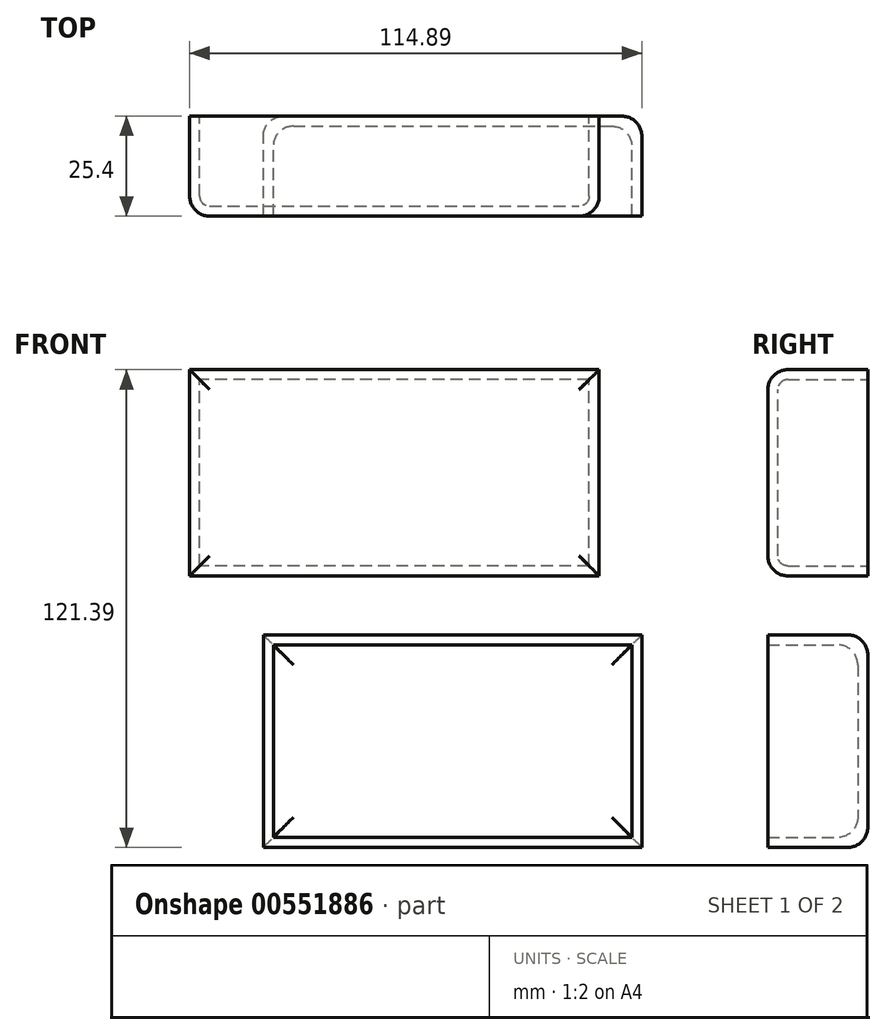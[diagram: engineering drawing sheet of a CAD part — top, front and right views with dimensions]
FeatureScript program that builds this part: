
annotation { "Feature Type Name" : "Feature", "Feature Type Description" : "" }
export const myFeature = defineFeature(function(context is Context, id is Id, definition is map)
    precondition{}
    {
        {
            var Q0;
            Q0=qCreatedBy(makeId("Front.planeOp"),FACE);
            var sketch = newSketch(context, id + "F0", { "sketchPlane" : qUnion([Q0])});
            skLineSegment(sketch, "E0.bottom", {"start": v(29.76, 10.05) * mm, "end": v(-74.3, 10.05) * mm});
            skLineSegment(sketch, "E0.top", {"start": v(29.76, 62.47) * mm, "end": v(-74.3, 62.47) * mm});
            skLineSegment(sketch, "E0.left", {"start": v(29.76, 10.05) * mm, "end": v(29.76, 62.47) * mm});
            skLineSegment(sketch, "E0.right", {"start": v(-74.3, 10.05) * mm, "end": v(-74.3, 62.47) * mm});
            skPoint(sketch, "E0.middle", {"position": v(-22.27, 36.26) * mm});
            skSolve(sketch);
        }
        {
            var Q0;
            Q0 = qSketchRegion(id + "F0", true);
            extrude(context, id + "F1", {"entities" : qUnion([Q0]), "depth" : 25.4 * mm, "offsetDistance" : 25.4 * mm});
        }
        {
            var Q0;
            Q0=makeQuery(id+"F1.opExtrude","CAP_FACE",FACE,{"disambiguationData":[OSD([sQuery(id+"F0.wireOp",EDGE,"E0.bottom"),sQuery(id+"F0.wireOp",EDGE,"E0.top"),sQuery(id+"F0.wireOp",EDGE,"E0.left"),sQuery(id+"F0.wireOp",EDGE,"E0.right")])],"isStart":false});
            fillet(context, id + "F2", {"entities" : qUnion([Q0]), "radius" : 5.08 * mm, "tangentPropagation" : true, "allowEdgeOverflow" : false});
        }
        {
            var Q0;
            Q0=makeQuery(id+"F1.opExtrude","CAP_FACE",FACE,{"disambiguationData":[OSD([sQuery(id+"F0.wireOp",EDGE,"E0.bottom"),sQuery(id+"F0.wireOp",EDGE,"E0.top"),sQuery(id+"F0.wireOp",EDGE,"E0.left"),sQuery(id+"F0.wireOp",EDGE,"E0.right")])],"isStart":true});
            shell(context, id + "F3", {"entities" : qUnion([Q0]), "thickness" : 2.54 * mm});
        }
        {
            var Q0;
            Q0=qCreatedBy(makeId("Front.planeOp"),FACE);
            var sketch = newSketch(context, id + "F4", { "sketchPlane" : qUnion([Q0])});
            skLineSegment(sketch, "E1.bottom", {"start": v(-55.57, -4.93) * mm, "end": v(40.6, -4.93) * mm});
            skLineSegment(sketch, "E1.top", {"start": v(-55.57, -58.92) * mm, "end": v(40.6, -58.92) * mm});
            skLineSegment(sketch, "E1.left", {"start": v(-55.57, -4.93) * mm, "end": v(-55.57, -58.92) * mm});
            skLineSegment(sketch, "E1.right", {"start": v(40.6, -4.93) * mm, "end": v(40.6, -58.92) * mm});
            skPoint(sketch, "E1.middle", {"position": v(-7.49, -31.93) * mm});
            skSolve(sketch);
        }
        {
            var Q0;
            Q0=makeQuery(id+"F4.imprint","IMPRINT",FACE,{"disambiguationData":[TD([[makeQuery(id+"F4.imprint","IMPRINT",EDGE,{"derivedFrom":sQuery(id+"F4.wireOp",EDGE,"E1.bottom")}),-1.0]])]});
            extrude(context, id + "F5", {"entities" : qUnion([Q0]), "depth" : 25.4 * mm, "offsetDistance" : 25.4 * mm});
        }
        {
            var Q0;
            Q0=makeQuery(id+"F5.opExtrude","CAP_FACE",FACE,{"disambiguationData":[OSD([sQuery(id+"F4.wireOp",EDGE,"E1.bottom"),sQuery(id+"F4.wireOp",EDGE,"E1.top"),sQuery(id+"F4.wireOp",EDGE,"E1.left"),sQuery(id+"F4.wireOp",EDGE,"E1.right")])],"isStart":false});
            shell(context, id + "F6", {"entities" : qUnion([Q0]), "thickness" : 2.54 * mm});
        }
        {
            var Q0;
            Q0=makeQuery(id+"F6.opShell","OFFSET_FACE",FACE,{"disambiguationData":[OSD([sQuery(id+"F4.wireOp",EDGE,"E1.bottom"),sQuery(id+"F4.wireOp",EDGE,"E1.top"),sQuery(id+"F4.wireOp",EDGE,"E1.left"),sQuery(id+"F4.wireOp",EDGE,"E1.right")])]});
            fillet(context, id + "F7", {"entities" : qUnion([Q0]), "radius" : 5.08 * mm, "tangentPropagation" : true, "allowEdgeOverflow" : false});
        }
        {
            var Q0;
            Q0=makeQuery(id+"F5.opExtrude","CAP_FACE",FACE,{"disambiguationData":[OSD([sQuery(id+"F4.wireOp",EDGE,"E1.bottom"),sQuery(id+"F4.wireOp",EDGE,"E1.top"),sQuery(id+"F4.wireOp",EDGE,"E1.left"),sQuery(id+"F4.wireOp",EDGE,"E1.right")])],"isStart":true});
            fillet(context, id + "F8", {"entities" : qUnion([Q0]), "radius" : 5.08 * mm, "tangentPropagation" : true, "allowEdgeOverflow" : false});
        }
    });
